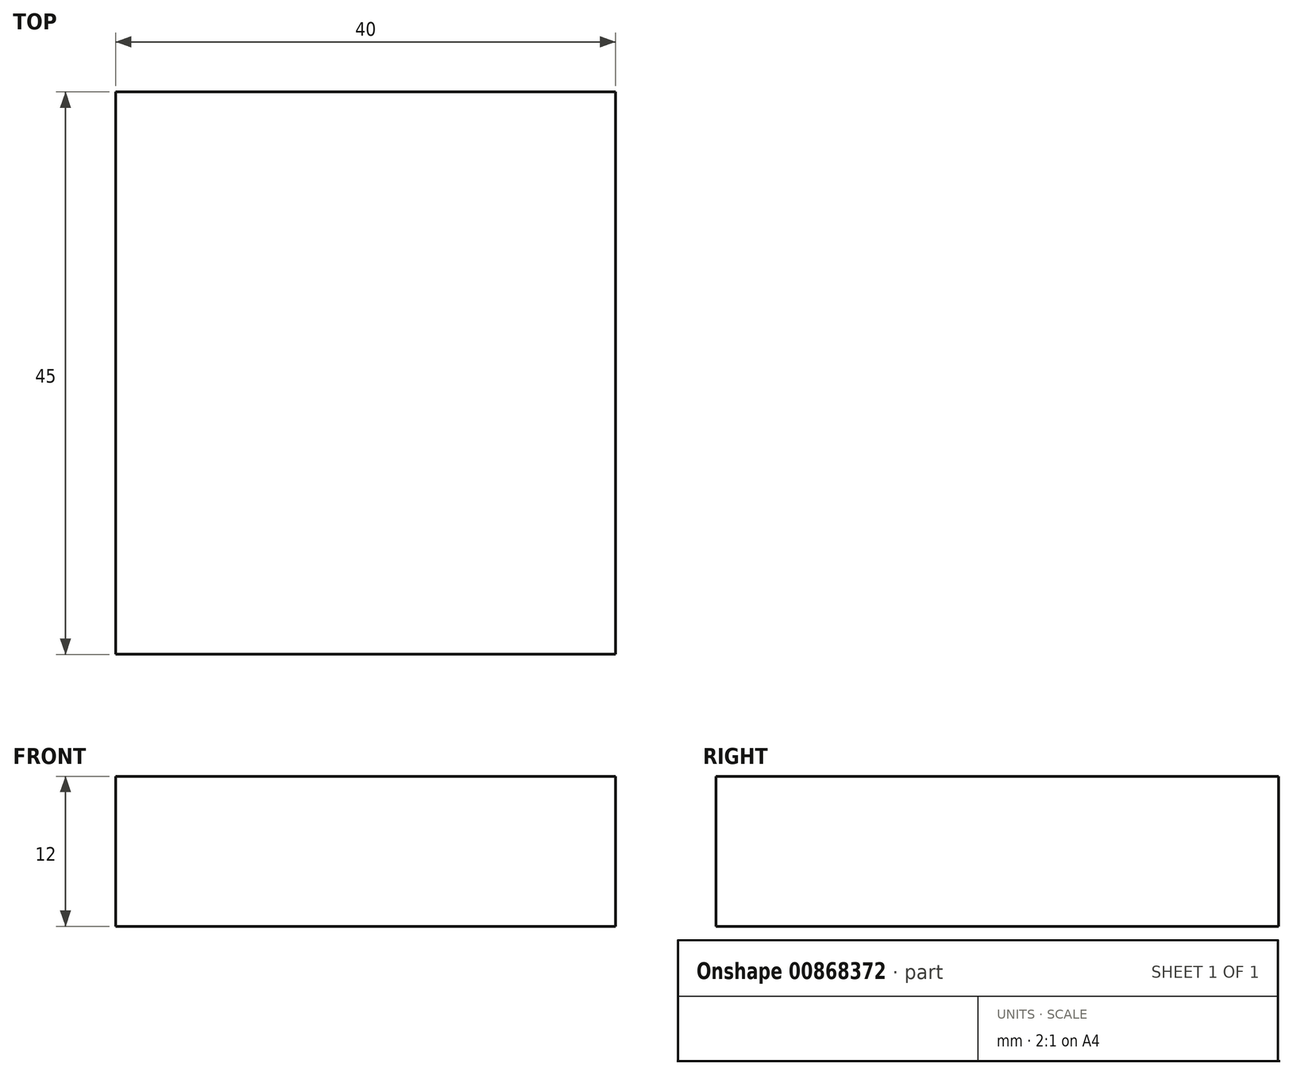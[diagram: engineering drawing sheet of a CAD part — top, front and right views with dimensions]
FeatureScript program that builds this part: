
annotation { "Feature Type Name" : "Feature", "Feature Type Description" : "" }
export const myFeature = defineFeature(function(context is Context, id is Id, definition is map)
    precondition{}
    {
        {
            var Q0;
            Q0=qCreatedBy(makeId("Top.planeOp"),FACE);
            var sketch = newSketch(context, id + "F0", { "sketchPlane" : qUnion([Q0])});
            skLineSegment(sketch, "E0.bottom", {"start": v(20, 25.85) * mm, "end": v(-20, 25.85) * mm});
            skLineSegment(sketch, "E0.top", {"start": v(20, -19.15) * mm, "end": v(-20, -19.15) * mm});
            skLineSegment(sketch, "E0.left", {"start": v(20, 25.85) * mm, "end": v(20, -19.15) * mm});
            skLineSegment(sketch, "E0.right", {"start": v(-20, 25.85) * mm, "end": v(-20, -19.15) * mm});
            skPoint(sketch, "E0.middle", {"position": v(0, 3.35) * mm});
            skSolve(sketch);
        }
        {
            var Q0;
            Q0=makeQuery(id+"F0.imprint","IMPRINT",FACE,{"disambiguationData":[TD([[makeQuery(id+"F0.imprint","IMPRINT",EDGE,{"derivedFrom":sQuery(id+"F0.wireOp",EDGE,"E0.bottom")}),1.0]])]});
            extrude(context, id + "F1", {"entities" : qUnion([Q0]), "depth" : 12 * mm, "offsetDistance" : 25 * mm});
        }
    });
